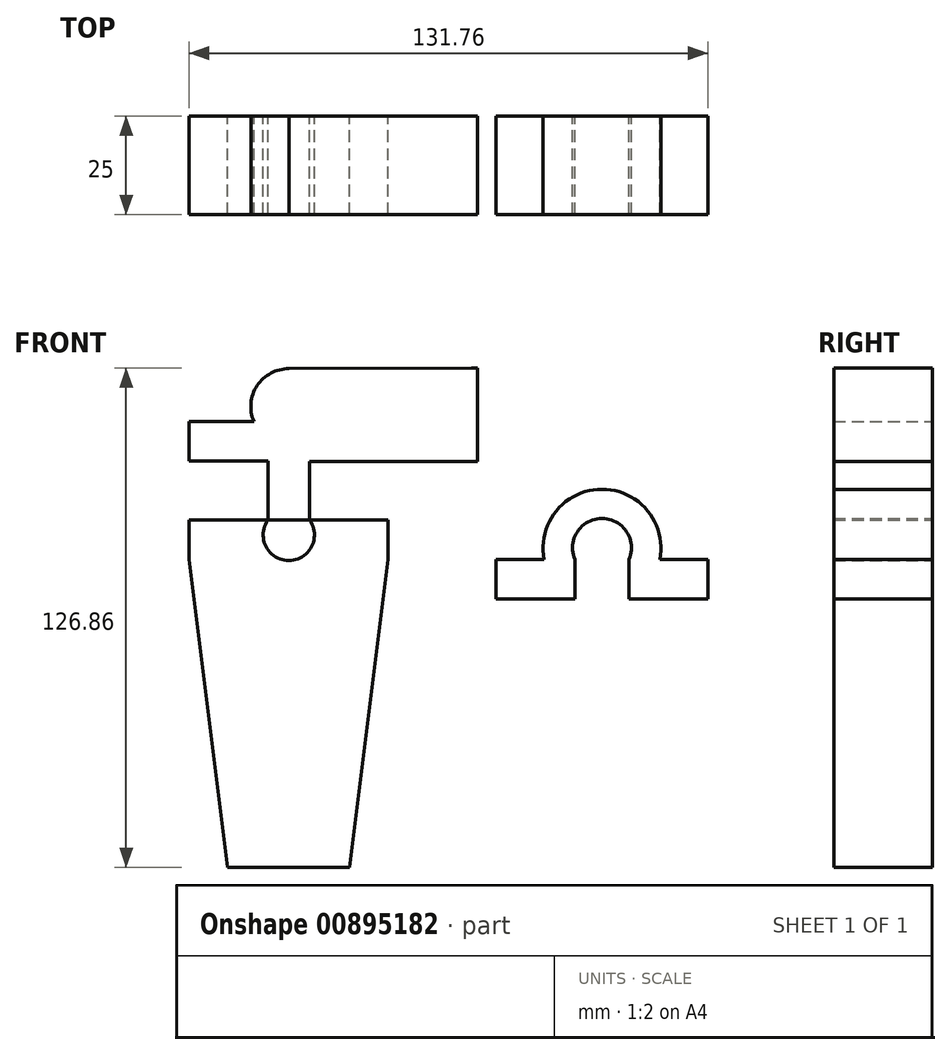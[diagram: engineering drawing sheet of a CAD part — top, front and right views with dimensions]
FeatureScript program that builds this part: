
annotation { "Feature Type Name" : "Feature", "Feature Type Description" : "" }
export const myFeature = defineFeature(function(context is Context, id is Id, definition is map)
    precondition{}
    {
        {
            var Q0;
            Q0=qCreatedBy(makeId("Front.planeOp"),FACE);
            var sketch = newSketch(context, id + "F0", { "sketchPlane" : qUnion([Q0])});
            skArc(sketch, "E0", {"start": v(-36.53, 34.89) * mm, "mid": v(-41.63, 45.26) * mm, "end": v(-47.09, 35.07) * mm});
            skLineSegment(sketch, "E1", {"start": v(-41.74, 38.77) * mm, "end": v(-41.63, -6.97) * mm});
            skPoint(sketch, "E1.endSnap0", {"position": v(-41.63, 45.26) * mm});
            skLineSegment(sketch, "E2", {"start": v(-41.63, -6.97) * mm, "end": v(-41.77, 48.53) * mm});
            skArc(sketch, "E3", {"start": v(-33.04, 35.07) * mm, "mid": v(-41.85, 48.47) * mm, "end": v(-50.66, 35.07) * mm});
            skLineSegment(sketch, "E4.bottom", {"start": v(-47.09, 35.07) * mm, "end": v(-67.09, 35.07) * mm});
            skLineSegment(sketch, "E4.top", {"start": v(-47.09, 25.07) * mm, "end": v(-67.09, 25.07) * mm});
            skLineSegment(sketch, "E4.left", {"start": v(-47.09, 35.07) * mm, "end": v(-47.09, 25.07) * mm});
            skLineSegment(sketch, "E4.right", {"start": v(-67.09, 35.07) * mm, "end": v(-67.09, 25.07) * mm});
            skLineSegment(sketch, "E5.bottom", {"start": v(-36.53, 34.89) * mm, "end": v(-16.53, 34.89) * mm});
            skLineSegment(sketch, "E5.top", {"start": v(-36.53, 24.89) * mm, "end": v(-16.53, 24.89) * mm});
            skLineSegment(sketch, "E5.left", {"start": v(-36.53, 34.89) * mm, "end": v(-36.53, 24.89) * mm});
            skLineSegment(sketch, "E5.right", {"start": v(-16.53, 34.89) * mm, "end": v(-16.53, 24.89) * mm});
            skLineSegment(sketch, "E6.bottom", {"start": v(-67.09, 10) * mm, "end": v(-16.53, 10) * mm});
            skLineSegment(sketch, "E6.top", {"start": v(-67.09, 0) * mm, "end": v(-16.53, 0) * mm});
            skLineSegment(sketch, "E6.left", {"start": v(-67.09, 10) * mm, "end": v(-67.09, 0) * mm});
            skLineSegment(sketch, "E6.right", {"start": v(-16.53, 10) * mm, "end": v(-16.53, 0) * mm});
            skLineSegment(sketch, "E7", {"start": v(-47.09, 25.07) * mm, "end": v(-36.53, 24.89) * mm});
            skLineSegment(sketch, "E8", {"start": v(-41.63, -6.97) * mm, "end": v(-41.63, -35.45) * mm});
            skLineSegment(sketch, "E9", {"start": v(-41.77, 48.53) * mm, "end": v(4.57, 48.64) * mm});
            skLineSegment(sketch, "E10", {"start": v(-16.53, 24.89) * mm, "end": v(6.08, 24.89) * mm});
            skLineSegment(sketch, "E11", {"start": v(6.08, 24.89) * mm, "end": v(6.08, 48.64) * mm});
            skLineSegment(sketch, "E12", {"start": v(6.08, 48.64) * mm, "end": v(4.57, 48.64) * mm});
            skLineSegment(sketch, "E13", {"start": v(-16.53, 10) * mm, "end": v(6.84, 10) * mm});
            skLineSegment(sketch, "E14", {"start": v(6.84, 10) * mm, "end": v(6.84, -78.22) * mm});
            skLineSegment(sketch, "E15", {"start": v(6.84, -78.22) * mm, "end": v(-73.01, -78.22) * mm});
            skLineSegment(sketch, "E16", {"start": v(-41.63, -35.45) * mm, "end": v(-41.63, -78.22) * mm});
            skLineSegment(sketch, "E17", {"start": v(-47.09, 25.07) * mm, "end": v(-47.09, 10) * mm});
            skLineSegment(sketch, "E18", {"start": v(-36.53, 24.89) * mm, "end": v(-36.5, 10) * mm});
            skArc(sketch, "E19", {"start": v(-47.09, 10) * mm, "mid": v(-41.8, -0.27) * mm, "end": v(-36.5, 10) * mm});
            skLineSegment(sketch, "E20", {"start": v(-67.09, 10) * mm, "end": v(-57.3, 0) * mm});
            skLineSegment(sketch, "E21", {"start": v(-16.53, 10) * mm, "end": v(-26.33, 0) * mm});
            skLineSegment(sketch, "E22.bottom", {"start": v(-57.3, 0) * mm, "end": v(-26.33, 0) * mm});
            skLineSegment(sketch, "E22.top", {"start": v(-57.3, -78.22) * mm, "end": v(-26.33, -78.22) * mm});
            skLineSegment(sketch, "E22.left", {"start": v(-57.3, 0) * mm, "end": v(-57.3, -78.22) * mm});
            skLineSegment(sketch, "E22.right", {"start": v(-26.33, 0) * mm, "end": v(-26.33, -78.22) * mm});
            skLineSegment(sketch, "E23", {"start": v(-67.09, 0) * mm, "end": v(-57.3, -78.22) * mm});
            skLineSegment(sketch, "E24", {"start": v(-16.53, 0) * mm, "end": v(-26.33, -78.22) * mm});
            skArc(sketch, "E25", {"start": v(44.67, 0) * mm, "mid": v(37.77, 10.43) * mm, "end": v(30.87, 0) * mm});
            skArc(sketch, "E26", {"start": v(52.5, 0) * mm, "mid": v(37.77, 17.84) * mm, "end": v(23.05, 0) * mm});
            skLineSegment(sketch, "E27.bottom", {"start": v(30.87, 0) * mm, "end": v(10.87, 0) * mm});
            skLineSegment(sketch, "E27.top", {"start": v(30.87, -10) * mm, "end": v(10.87, -10) * mm});
            skLineSegment(sketch, "E27.left", {"start": v(30.87, 0) * mm, "end": v(30.87, -10) * mm});
            skLineSegment(sketch, "E27.right", {"start": v(10.87, 0) * mm, "end": v(10.87, -10) * mm});
            skLineSegment(sketch, "E28.bottom", {"start": v(44.67, 0) * mm, "end": v(64.67, 0) * mm});
            skLineSegment(sketch, "E28.top", {"start": v(44.67, -10) * mm, "end": v(64.67, -10) * mm});
            skLineSegment(sketch, "E28.left", {"start": v(44.67, 0) * mm, "end": v(44.67, -10) * mm});
            skLineSegment(sketch, "E28.right", {"start": v(64.67, 0) * mm, "end": v(64.67, -10) * mm});
            skSolve(sketch);
        }
        {
            var Q0;
            Q0=makeQuery(id+"F0.imprint","IMPRINT",FACE,{"disambiguationData":[TD([[makeQuery(id+"F0.imprint","IMPRINT",EDGE,{"derivedFrom":sQuery(id+"F0.wireOp",EDGE,"E4.top")}),-1.0]])]});
            var Q1;
            {var subQ3=sQuery(id+"F0.wireOp",EDGE,"E2");var subQ5=sQuery(id+"F0.wireOp",EDGE,"E3");var subQ7=makeQuery(id+"F0.imprint","INTERSECT",VERTEX,{"derivedFrom":[subQ3,subQ5]});Q1=makeQuery(id+"F0.imprint","IMPRINT",FACE,{"disambiguationData":[TD([[makeQuery(id+"F0.imprint","IMPRINT",EDGE,{"disambiguationData":[TD([[subQ7,1.0]])],"derivedFrom":subQ3}),1.0]])]});}
            var Q2;
            {var subQ0=sQuery(id+"F0.wireOp",EDGE,"E4.left");Q2=makeQuery(id+"F0.imprint","IMPRINT",FACE,{"disambiguationData":[TD([[makeQuery(id+"F0.imprint","IMPRINT",EDGE,{"derivedFrom":subQ0}),1.0]])]});}
            var Q3;
            {var subQ0=sQuery(id+"F0.wireOp",EDGE,"E5.left");Q3=makeQuery(id+"F0.imprint","IMPRINT",FACE,{"disambiguationData":[TD([[makeQuery(id+"F0.imprint","IMPRINT",EDGE,{"derivedFrom":subQ0}),-1.0]])]});}
            var Q4;
            Q4=makeQuery(id+"F0.imprint","IMPRINT",FACE,{"disambiguationData":[TD([[makeQuery(id+"F0.imprint","IMPRINT",EDGE,{"derivedFrom":sQuery(id+"F0.wireOp",EDGE,"E5.bottom")}),-1.0]])]});
            var Q5;
            {var subQ0=sQuery(id+"F0.wireOp",EDGE,"E22.bottom");var subQ1=sQuery(id+"F0.wireOp",EDGE,"E2");var subQ2=makeQuery(id+"F0.imprint","INTERSECT",VERTEX,{"derivedFrom":[subQ1,subQ0]});Q5=makeQuery(id+"F0.imprint","IMPRINT",FACE,{"disambiguationData":[TD([[makeQuery(id+"F0.imprint","IMPRINT",EDGE,{"disambiguationData":[TD([[subQ2,-1.0]])],"derivedFrom":subQ1}),-1.0]])]});}
            var Q6;
            {var subQ0=sQuery(id+"F0.wireOp",EDGE,"E22.bottom");var subQ1=sQuery(id+"F0.wireOp",EDGE,"E2");var subQ2=makeQuery(id+"F0.imprint","INTERSECT",VERTEX,{"derivedFrom":[subQ1,subQ0]});Q6=makeQuery(id+"F0.imprint","IMPRINT",FACE,{"disambiguationData":[TD([[makeQuery(id+"F0.imprint","IMPRINT",EDGE,{"disambiguationData":[TD([[subQ2,-1.0]])],"derivedFrom":subQ1}),1.0]])]});}
            var Q7;
            {var subQ5=sQuery(id+"F0.wireOp",EDGE,"E17");Q7=makeQuery(id+"F0.imprint","IMPRINT",FACE,{"disambiguationData":[TD([[makeQuery(id+"F0.imprint","IMPRINT",EDGE,{"derivedFrom":subQ5}),1.0]])]});}
            var Q8;
            {var subQ5=sQuery(id+"F0.wireOp",EDGE,"E18");Q8=makeQuery(id+"F0.imprint","IMPRINT",FACE,{"disambiguationData":[TD([[makeQuery(id+"F0.imprint","IMPRINT",EDGE,{"derivedFrom":subQ5}),-1.0]])]});}
            var Q9;
            {var subQ0=sQuery(id+"F0.wireOp",EDGE,"E21");Q9=makeQuery(id+"F0.imprint","IMPRINT",FACE,{"disambiguationData":[TD([[makeQuery(id+"F0.imprint","IMPRINT",EDGE,{"derivedFrom":subQ0}),-1.0]])]});}
            var Q10;
            {var subQ2=sQuery(id+"F0.wireOp",EDGE,"E22.right");Q10=makeQuery(id+"F0.imprint","IMPRINT",FACE,{"disambiguationData":[TD([[makeQuery(id+"F0.imprint","IMPRINT",EDGE,{"derivedFrom":subQ2}),1.0]])]});}
            var Q11;
            {var subQ0=sQuery(id+"F0.wireOp",EDGE,"E20");Q11=makeQuery(id+"F0.imprint","IMPRINT",FACE,{"disambiguationData":[TD([[makeQuery(id+"F0.imprint","IMPRINT",EDGE,{"derivedFrom":subQ0}),1.0]])]});}
            var Q12;
            {var subQ0=sQuery(id+"F0.wireOp",EDGE,"E6.left");Q12=makeQuery(id+"F0.imprint","IMPRINT",FACE,{"disambiguationData":[TD([[makeQuery(id+"F0.imprint","IMPRINT",EDGE,{"derivedFrom":subQ0}),1.0]])]});}
            var Q13;
            {var subQ0=sQuery(id+"F0.wireOp",EDGE,"E6.right");Q13=makeQuery(id+"F0.imprint","IMPRINT",FACE,{"disambiguationData":[TD([[makeQuery(id+"F0.imprint","IMPRINT",EDGE,{"derivedFrom":subQ0}),-1.0]])]});}
            var Q14;
            {var subQ2=sQuery(id+"F0.wireOp",EDGE,"E22.left");Q14=makeQuery(id+"F0.imprint","IMPRINT",FACE,{"disambiguationData":[TD([[makeQuery(id+"F0.imprint","IMPRINT",EDGE,{"derivedFrom":subQ2}),-1.0]])]});}
            var Q15;
            {var subQ1=sQuery(id+"F0.wireOp",EDGE,"E8");Q15=makeQuery(id+"F0.imprint","IMPRINT",FACE,{"disambiguationData":[TD([[makeQuery(id+"F0.imprint","IMPRINT",EDGE,{"derivedFrom":subQ1}),-1.0]])]});}
            var Q16;
            {var subQ7=sQuery(id+"F0.wireOp",EDGE,"E8");Q16=makeQuery(id+"F0.imprint","IMPRINT",FACE,{"disambiguationData":[TD([[makeQuery(id+"F0.imprint","IMPRINT",EDGE,{"derivedFrom":subQ7}),1.0]])]});}
            extrude(context, id + "F1", {"entities" : qUnion([Q0, Q1, Q2, Q3, Q4, Q5, Q6, Q7, Q8, Q9, Q10, Q11, Q12, Q13, Q14, Q15, Q16]), "depth" : 25 * mm, "offsetDistance" : 25 * mm});
        }
        {
            var Q0;
            Q0=makeQuery(id+"F0.imprint","IMPRINT",FACE,{"disambiguationData":[TD([[makeQuery(id+"F0.imprint","IMPRINT",EDGE,{"derivedFrom":sQuery(id+"F0.wireOp",EDGE,"E27.top")}),-1.0]])]});
            var Q1;
            {var subQ0=sQuery(id+"F0.wireOp",EDGE,"E25");Q1=makeQuery(id+"F0.imprint","IMPRINT",FACE,{"disambiguationData":[TD([[makeQuery(id+"F0.imprint","IMPRINT",EDGE,{"derivedFrom":subQ0}),-1.0]])]});}
            var Q2;
            Q2=makeQuery(id+"F0.imprint","IMPRINT",FACE,{"disambiguationData":[TD([[makeQuery(id+"F0.imprint","IMPRINT",EDGE,{"derivedFrom":sQuery(id+"F0.wireOp",EDGE,"E28.top")}),1.0]])]});
            extrude(context, id + "F2", {"entities" : qUnion([Q0, Q1, Q2]), "depth" : 25 * mm, "offsetDistance" : 25 * mm});
        }
    });
